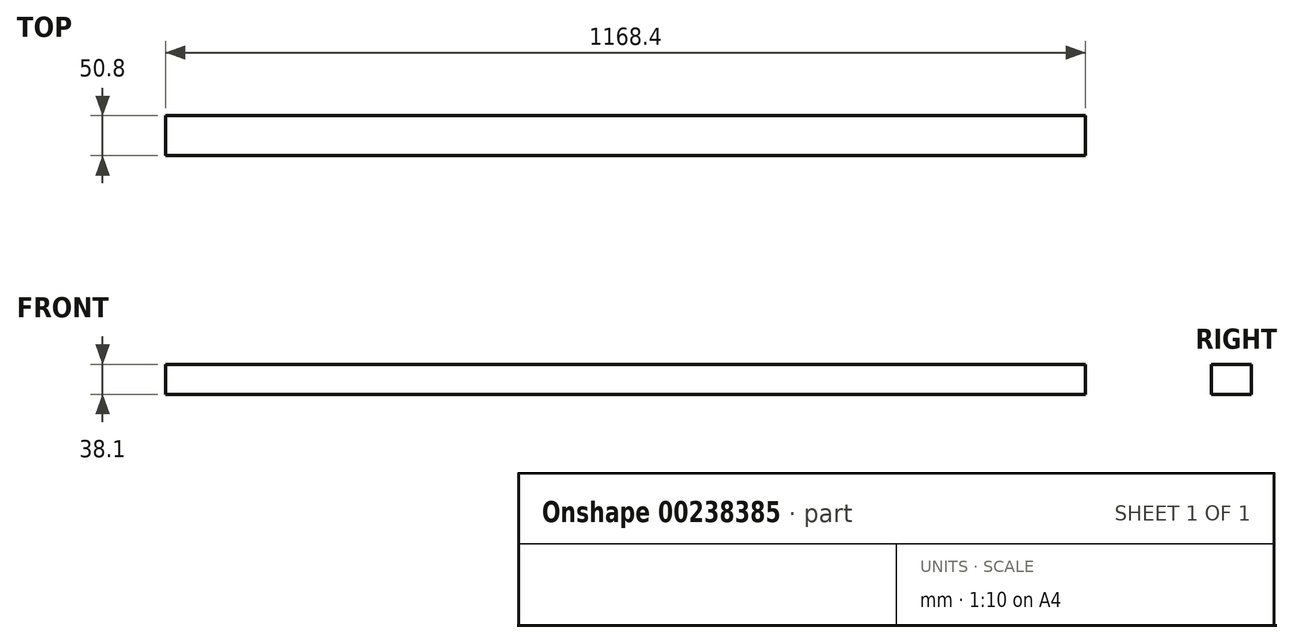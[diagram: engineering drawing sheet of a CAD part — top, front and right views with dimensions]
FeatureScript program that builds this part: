
annotation { "Feature Type Name" : "Feature", "Feature Type Description" : "" }
export const myFeature = defineFeature(function(context is Context, id is Id, definition is map)
    precondition{}
    {
        {
            var Q0;
            Q0=qCreatedBy(makeId("Top.planeOp"),FACE);
            var sketch = newSketch(context, id + "F0", { "sketchPlane" : qUnion([Q0])});
            skLineSegment(sketch, "E0.bottom", {"start": v(584.2, 25.4) * mm, "end": v(-584.2, 25.4) * mm});
            skLineSegment(sketch, "E0.top", {"start": v(584.2, -25.4) * mm, "end": v(-584.2, -25.4) * mm});
            skLineSegment(sketch, "E0.left", {"start": v(584.2, 25.4) * mm, "end": v(584.2, -25.4) * mm});
            skLineSegment(sketch, "E0.right", {"start": v(-584.2, 25.4) * mm, "end": v(-584.2, -25.4) * mm});
            skPoint(sketch, "E0.middle", {"position": v(0, 0) * mm});
            skSolve(sketch);
        }
        {
            var Q0;
            Q0 = qSketchRegion(id + "F0", true);
            extrude(context, id + "F1", {"entities" : qUnion([Q0]), "depth" : 38.1 * mm});
        }
    });
